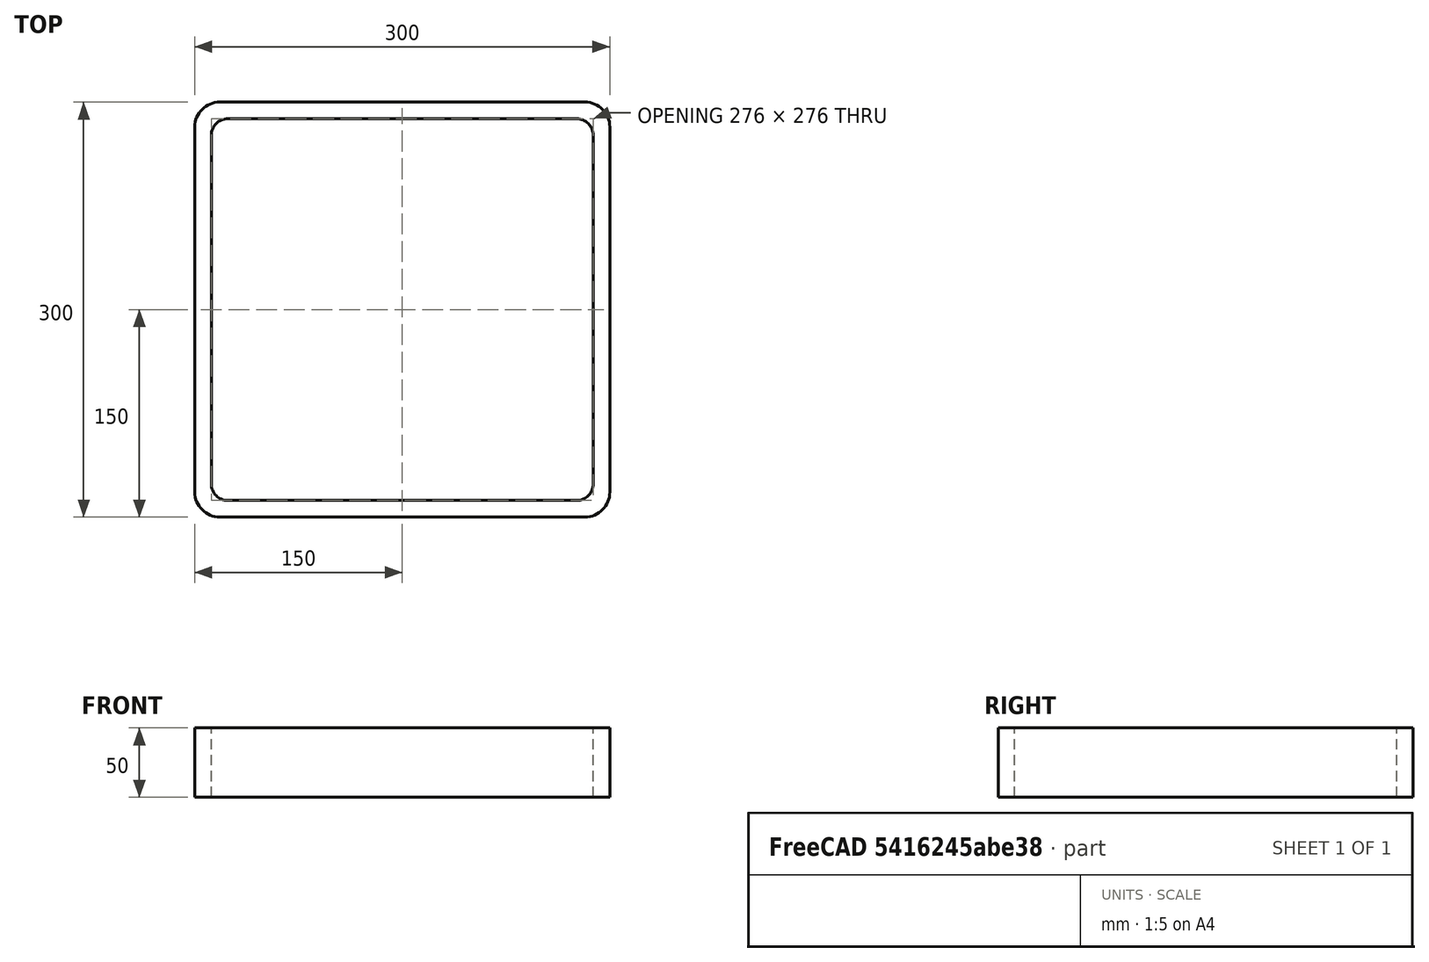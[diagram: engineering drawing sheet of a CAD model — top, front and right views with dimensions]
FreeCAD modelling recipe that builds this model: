
FCSTD DOCUMENT  (FreeCAD 0.15R4671 (Git))
Label: Square hollow section 300x300x12 EN10219 S235JRH
License: All rights reserved
LicenseURL: http://en.wikipedia.org/wiki/All_rights_reserved
objects: Sketcher::SketchObject×1, Part::Extrusion×1
note: 2 computed .brp shape members not serialized (recipe doc carries the construction recipe); baked Part::Feature solids carry a one-line shape summary decoded from their .brp

FEATURE [Sketcher::SketchObject] Sketch
  sketch-geometry (16):
    g0: LineSegment StartX=-126 StartY=138 StartZ=0 EndX=126 EndY=138 EndZ=0
    g1: LineSegment StartX=138 StartY=126 StartZ=0 EndX=138 EndY=-126 EndZ=0
    g2: LineSegment StartX=126 StartY=-138 StartZ=0 EndX=-126 EndY=-138 EndZ=0
    g3: LineSegment StartX=-138 StartY=-126 StartZ=0 EndX=-138 EndY=126 EndZ=0
    g4: LineSegment StartX=-132 StartY=150 StartZ=0 EndX=132 EndY=150 EndZ=0
    g5: LineSegment StartX=150 StartY=132 StartZ=0 EndX=150 EndY=-132 EndZ=0
    g6: LineSegment StartX=132 StartY=-150 StartZ=0 EndX=-132 EndY=-150 EndZ=0
    g7: LineSegment StartX=-150 StartY=-132 StartZ=0 EndX=-150 EndY=132 EndZ=0
    g8: ArcOfCircle CenterX=-126 CenterY=126 CenterZ=0 NormalX=0 NormalY=0 NormalZ=1 Radius=12 StartAngle=1.5708 EndAngle=3.14159
    g9: ArcOfCircle CenterX=126 CenterY=126 CenterZ=0 NormalX=0 NormalY=0 NormalZ=1 Radius=12 StartAngle=0 EndAngle=1.5708
    g10: ArcOfCircle CenterX=126 CenterY=-126 CenterZ=0 NormalX=0 NormalY=0 NormalZ=1 Radius=12 StartAngle=4.71239 EndAngle=6.28319
    g11: ArcOfCircle CenterX=-126 CenterY=-126 CenterZ=0 NormalX=0 NormalY=0 NormalZ=1 Radius=12 StartAngle=3.14159 EndAngle=4.71239
    g12: ArcOfCircle CenterX=132 CenterY=132 CenterZ=0 NormalX=0 NormalY=0 NormalZ=1 Radius=18 StartAngle=0 EndAngle=1.5708
    g13: ArcOfCircle CenterX=132 CenterY=-132 CenterZ=0 NormalX=0 NormalY=0 NormalZ=1 Radius=18 StartAngle=4.71239 EndAngle=6.28319
    g14: ArcOfCircle CenterX=-132 CenterY=-132 CenterZ=0 NormalX=0 NormalY=0 NormalZ=1 Radius=18 StartAngle=3.14159 EndAngle=4.71239
    g15: ArcOfCircle CenterX=-132 CenterY=132 CenterZ=0 NormalX=0 NormalY=0 NormalZ=1 Radius=18 StartAngle=1.5708 EndAngle=3.14159
  constraints (36):
    c: Horizontal(g2)
    c: Vertical(g3)
    c: Horizontal(g6)
    c: Vertical(g7)
    c: Tangent(g3,g8) = 1.5708
    c: Tangent(g0,g8) = 1.5708
    c: Tangent(g0,g9) = 1.5708
    c: Tangent(g1,g9) = 1.5708
    c: Tangent(g1,g10) = 1.5708
    c: Tangent(g2,g10) = 1.5708
    c: Tangent(g2,g11) = 1.5708
    c: Tangent(g3,g11) = 1.5708
    c: Tangent(g4,g12) = 1.5708
    c: Tangent(g5,g12) = 1.5708
    c: Tangent(g5,g13) = 1.5708
    c: Tangent(g6,g13) = 1.5708
    c: Tangent(g6,g14) = 1.5708
    c: Tangent(g7,g14) = 1.5708
    c: Tangent(g7,g15) = 1.5708
    c: Tangent(g4,g15) = 1.5708
    c: Equal(g9,g8)
    c: Equal(g9,g11)
    c: Equal(g9,g10)
    c: Equal(g12,g15)
    c: Equal(g12,g14)
    c: Equal(g12,g13)
    c: Symmetric(g4,g6,g-1)
    c: Symmetric(g7,g5,g-2)
    c: DistanceY(g4,g6) = -300
    c: DistanceX(g7,g5) = 300
    c: Symmetric(g3,g1,g-2)
    c: Symmetric(g0,g2,g-1)
    c: DistanceY(g0,g4) = 12
    c: DistanceX(g5,g1) = -12
    c: Radius(g9) = 12
    c: Radius(g12) = 18
FEATURE [Part::Extrusion] Extrude  label="Square hollow section 300x300x12 EN10219 S235JRH"
  Base = -> Sketch
  Dir = (0,0,50)
  Solid = true
